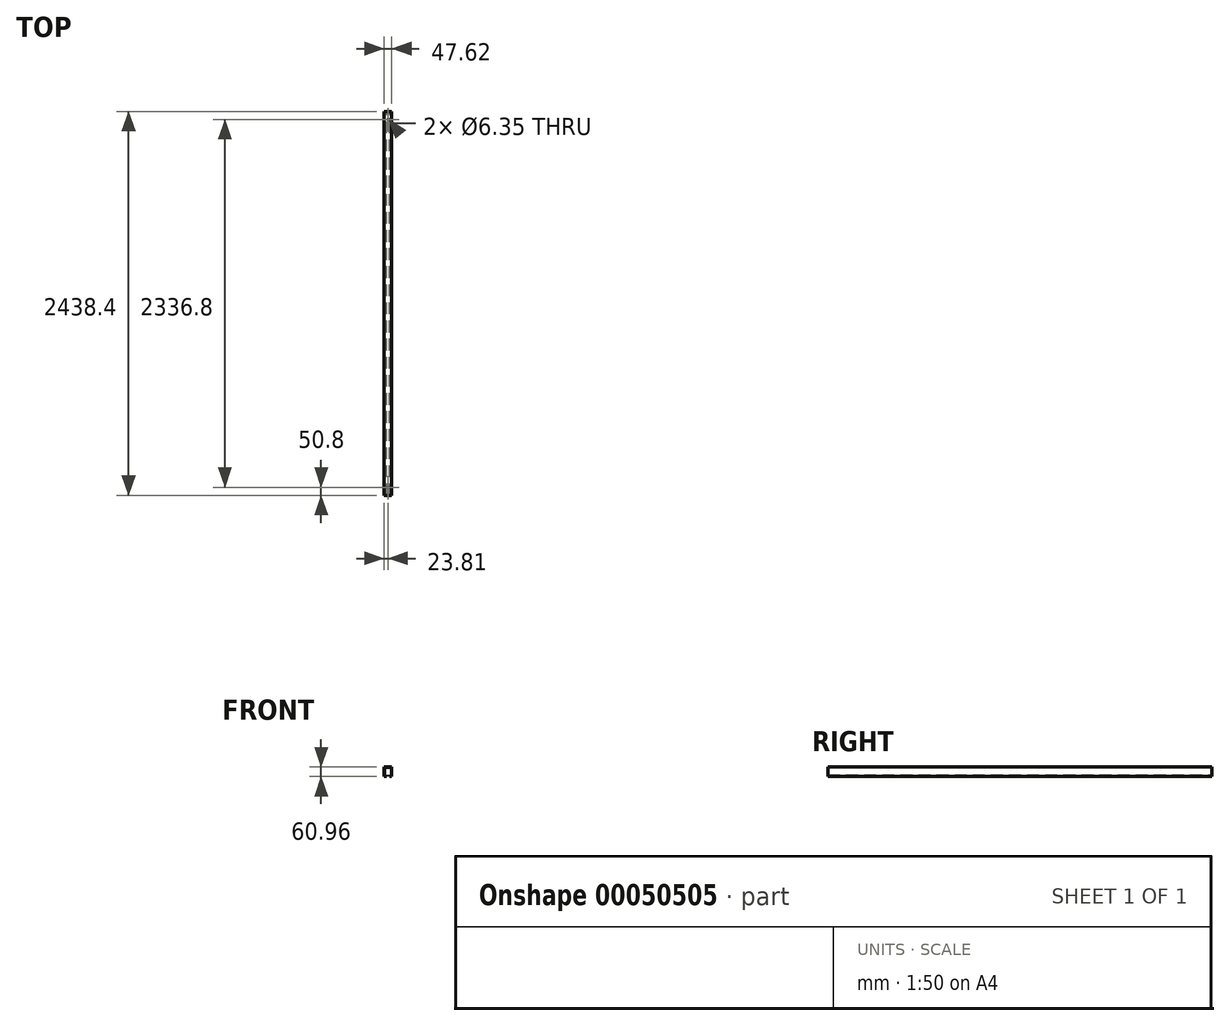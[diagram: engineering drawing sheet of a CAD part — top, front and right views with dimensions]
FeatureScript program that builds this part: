
annotation { "Feature Type Name" : "Feature", "Feature Type Description" : "" }
export const myFeature = defineFeature(function(context is Context, id is Id, definition is map)
    precondition{}
    {
        {
            var Q0;
            Q0=qCreatedBy(makeId("Front.planeOp"),FACE);
            var sketch = newSketch(context, id + "F0", { "sketchPlane" : qUnion([Q0])});
            skLineSegment(sketch, "E0.rect.bottom", {"start": v(23.81, 30.48) * mm, "end": v(-23.81, 30.48) * mm});
            skLineSegment(sketch, "E0.rect.left", {"start": v(23.81, 30.48) * mm, "end": v(23.81, -30.48) * mm});
            skLineSegment(sketch, "E0.rect.right", {"start": v(-23.81, 30.48) * mm, "end": v(-23.81, -30.48) * mm});
            skPoint(sketch, "E0.rect.middle", {"position": v(0, 0) * mm});
            skLineSegment(sketch, "E1.bottom", {"start": v(-22.16, 28.77) * mm, "end": v(22.16, 28.77) * mm});
            skLineSegment(sketch, "E1.top", {"start": v(-22.16, -28.77) * mm, "end": v(-10.29, -28.77) * mm});
            skLineSegment(sketch, "E1.left", {"start": v(-22.16, 28.77) * mm, "end": v(-22.16, -28.77) * mm});
            skLineSegment(sketch, "E1.right", {"start": v(22.16, 28.77) * mm, "end": v(22.16, -28.77) * mm});
            skLineSegment(sketch, "E2", {"start": v(-10.29, -28.77) * mm, "end": v(-10.29, -20.17) * mm});
            skLineSegment(sketch, "E3", {"start": v(-10.29, -20.17) * mm, "end": v(-8.57, -20.17) * mm});
            skLineSegment(sketch, "E4", {"start": v(-8.57, -20.17) * mm, "end": v(-8.57, -30.48) * mm});
            skLineSegment(sketch, "E5", {"start": v(8.57, -30.48) * mm, "end": v(8.57, -20.17) * mm});
            skLineSegment(sketch, "E6", {"start": v(8.57, -20.17) * mm, "end": v(10.29, -20.17) * mm});
            skLineSegment(sketch, "E7", {"start": v(10.29, -20.17) * mm, "end": v(10.29, -28.77) * mm});
            skLineSegment(sketch, "E8.trimOffspring", {"start": v(10.29, -28.77) * mm, "end": v(22.16, -28.77) * mm});
            skLineSegment(sketch, "E9.trimOffspring", {"start": v(-8.57, -30.48) * mm, "end": v(-23.81, -30.48) * mm});
            skLineSegment(sketch, "E10", {"start": v(23.81, -30.48) * mm, "end": v(8.57, -30.48) * mm});
            skSolve(sketch);
        }
        {
            var Q0;
            Q0 = qSketchRegion(id + "F0", true);
            extrude(context, id + "F1", {"entities" : qUnion([Q0]), "endBound" : BoundingType.SYMMETRIC, "depth" : 2438.4 * mm});
        }
        {
            var Q0;
            Q0=makeQuery(id+"F1.opExtrude","SWEPT_FACE",FACE,{"disambiguationData":[OSD([sQuery(id+"F0.wireOp",EDGE,"E0.rect.bottom")])]});
            var sketch = newSketch(context, id + "F2", { "sketchPlane" : qUnion([Q0])});
            skCircle(sketch, "E11", {"center": v(0, 1168.4) * mm, "radius": 3.18 * mm});
            skCircle(sketch, "E12", {"center": v(0, -1168.4) * mm, "radius": 3.18 * mm});
            skLineSegment(sketch, "E13", {"start": v(0, 1168.4) * mm, "end": v(0, 0) * mm, "construction": true});
            skLineSegment(sketch, "E14", {"start": v(0, 0) * mm, "end": v(0, -1168.4) * mm, "construction": true});
            skSolve(sketch);
        }
        {
            var Q0;
            Q0 = qSketchRegion(id + "F2", true);
            extrude(context, id + "F3", {"entities" : qUnion([Q0]), "operationType" : NewBodyOperationType.REMOVE, "endBound" : BoundingType.UP_TO_NEXT, "oppositeDirection" : true, "depth" : 25.4 * mm});
        }
    });
